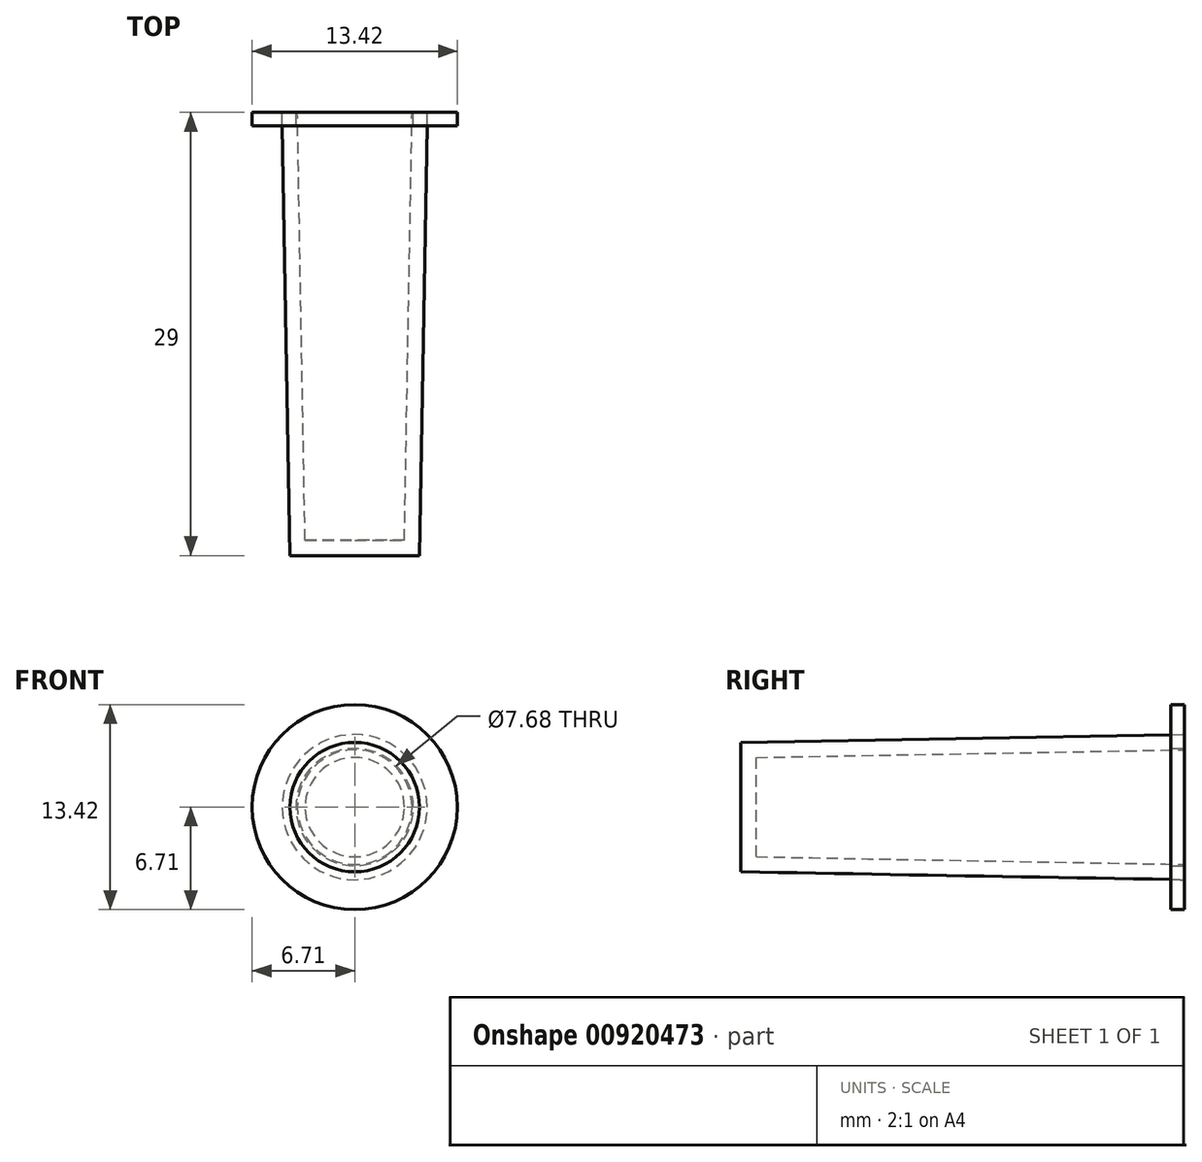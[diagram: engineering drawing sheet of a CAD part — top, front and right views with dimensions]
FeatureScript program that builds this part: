
annotation { "Feature Type Name" : "Feature", "Feature Type Description" : "" }
export const myFeature = defineFeature(function(context is Context, id is Id, definition is map)
    precondition{}
    {
        {
            var Q0;
            Q0=qCreatedBy(makeId("Front.planeOp"),FACE);
            var sketch = newSketch(context, id + "F0", { "sketchPlane" : qUnion([Q0])});
            skCircle(sketch, "E0", {"center": v(0, 0) * mm, "radius": 3.75 * mm});
            skSolve(sketch);
        }
        {
            var Q0;
            Q0=qCreatedBy(makeId("Front.planeOp"),FACE);
            cPlane(context, id + "F1", {"entities" : qUnion([Q0]), "cplaneType" : CPlaneType.OFFSET, "offset" : 28 * mm, "width" : 150 * mm, "height" : 150 * mm});
        }
        {
            var Q0;
            Q0=qCreatedBy(id+"F1.planeOp",FACE);
            var sketch = newSketch(context, id + "F2", { "sketchPlane" : qUnion([Q0])});
            skCircle(sketch, "E1", {"center": v(0, 0) * mm, "radius": 3.25 * mm});
            skSolve(sketch);
        }
        {
            var Q0;
            Q0=makeQuery(id+"F0.imprint","IMPRINT",FACE,{"disambiguationData":[TD([[makeQuery(id+"F0.imprint","IMPRINT",EDGE,{"derivedFrom":sQuery(id+"F0.wireOp",EDGE,"E0")}),1.0]])]});
            var Q1;
            Q1=makeQuery(id+"F2.imprint","IMPRINT",FACE,{"disambiguationData":[TD([[makeQuery(id+"F2.imprint","IMPRINT",EDGE,{"derivedFrom":sQuery(id+"F2.wireOp",EDGE,"E1")}),1.0]])]});
            loft(context, id + "F3", {"sheetProfilesArray" : [{ "sheetProfileEntities" : qUnion([Q0]) }, { "sheetProfileEntities" : qUnion([Q1]) }]});
        }
        {
            var Q0;
            Q0=qCreatedBy(makeId("Right.planeOp"),FACE);
            var sketch = newSketch(context, id + "F4", { "sketchPlane" : qUnion([Q0])});
            skLineSegment(sketch, "E2.bottom", {"start": v(0, 3.84) * mm, "end": v(-0.87, 3.84) * mm});
            skLineSegment(sketch, "E2.top", {"start": v(0, 6.7) * mm, "end": v(-0.87, 6.7) * mm});
            skLineSegment(sketch, "E2.left", {"start": v(0, 3.84) * mm, "end": v(0, 6.7) * mm});
            skLineSegment(sketch, "E2.right", {"start": v(-0.87, 3.84) * mm, "end": v(-0.87, 6.7) * mm});
            skSolve(sketch);
        }
        {
            var Q0;
            Q0 = qSketchRegion(id + "F4", true);
            var Q1;
            Q1=makeQuery(id+"F3.opLoft","MID_CAP_EDGE",EDGE,{"disambiguationData":[OSD([sQuery(id+"F0.wireOp",EDGE,"E0")])],"capPos":0.0});
            revolve(context, id + "F5", {"surfaceOperationType" : NewSurfaceOperationType.NEW, "entities" : qUnion([Q0]), "axis" : qUnion([Q1]), "revolveType" : RevolveType.FULL});
        }
        {
            var Q0;
            Q0=makeQuery(id+"F3.opLoft","SWEPT_FACE",FACE,{"disambiguationData":[OSD([sQuery(id+"F0.wireOp",EDGE,"E0"),sQuery(id+"F2.wireOp",EDGE,"E1")])]});
            var Q1;
            Q1=makeQuery(id+"F3.opLoft","SWEPT_BODY",BODY,{"disambiguationData":[OSD([makeQuery(id+"F0.imprint","IMPRINT",FACE,{"disambiguationData":[TD([[makeQuery(id+"F0.imprint","IMPRINT",EDGE,{"derivedFrom":sQuery(id+"F0.wireOp",EDGE,"E0")}),1.0]])]}),makeQuery(id+"F2.imprint","IMPRINT",FACE,{"disambiguationData":[TD([[makeQuery(id+"F2.imprint","IMPRINT",EDGE,{"derivedFrom":sQuery(id+"F2.wireOp",EDGE,"E1")}),1.0]])]})])]});
            shell(context, id + "F6", {"isHollow" : true, "entities" : qUnion([Q0]), "parts" : qUnion([Q1]), "thickness" : 1 * mm, "oppositeDirection" : true});
        }
        {
            var Q0;
            Q0=qCreatedBy(makeId("Right.planeOp"),FACE);
            var sketch = newSketch(context, id + "F7", { "sketchPlane" : qUnion([Q0])});
            skLineSegment(sketch, "E3.bottom", {"start": v(0, 6.73) * mm, "end": v(1.2, 6.73) * mm});
            skLineSegment(sketch, "E3.top", {"start": v(0, -6.73) * mm, "end": v(1.2, -6.73) * mm});
            skLineSegment(sketch, "E3.left", {"start": v(0, 6.73) * mm, "end": v(0, -6.73) * mm});
            skLineSegment(sketch, "E3.right", {"start": v(1.2, 6.73) * mm, "end": v(1.2, -6.73) * mm});
            skSolve(sketch);
        }
        {
            var Q0;
            Q0 = qSketchRegion(id + "F7", true);
            extrude(context, id + "F8", {"entities" : qUnion([Q0]), "operationType" : NewBodyOperationType.REMOVE, "oppositeDirection" : true, "depth" : 25 * mm, "offsetDistance" : 25 * mm, "symmetric" : true});
        }
    });
